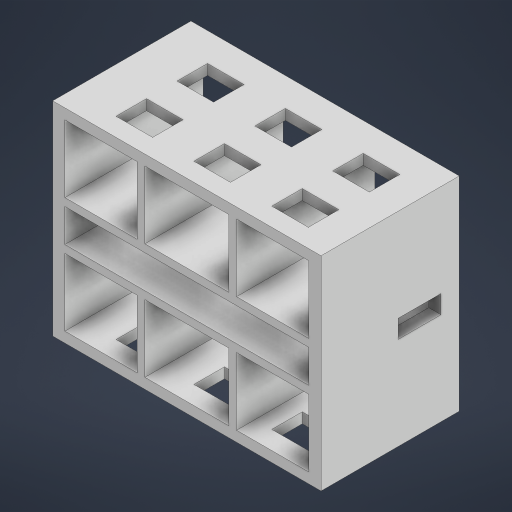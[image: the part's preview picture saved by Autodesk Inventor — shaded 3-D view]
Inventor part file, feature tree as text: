
AUTODESK INVENTOR PART (.ipt)
format: ipt  version: 2024.3 (Build 283343000, 343)  size: 326,656 bytes
history: native  units: mm
features: extrude x4, sketch x4
ambient origin geometry x8: Origin, YZ Plane, XZ Plane, XY Plane, X Axis, Y Axis, Z Axis, Center Point
bodies: Solid1 (feature_tree)
feature tree (8):
  extrude  "Extrusion1"  Depth=9000.0mm
  extrude  "Extrusion2"  Depth=10020.0mm
  extrude  "Extrusion4"  Depth=1800.0mm
  extrude  "Extrusion5"  Depth=1525.0mm
  sketch  "Sketch1"  dims[d0=12000.0mm d1=9000.0mm]
  sketch  "Sketch2"  dims[d2=13200.0mm d3=10020.0mm]
  sketch  "Sketch3"  dims[d4=6800.0mm d5=0.0mm d6=1800.0mm]
  sketch  "Sketch4"  dims[d7=1500.0mm d8=1525.0mm d9=1400.0mm d10=1800.0mm d11=1500.0mm d12=1500.0mm d13=1525.0mm d14=1800.0mm d15=1500.0mm d16=1800.0mm d17=1500.0mm d18=1500.0mm d19=1800.0mm d20=1500.0mm d21=1800.0mm d22=1500.0mm d23=1500.0mm d24=2030.0mm d25=2030.0mm d26=11000.0mm d27=0.0mm d32=90.0deg d39=3310.0mm d46=3555.0mm d47=380.0mm d50=380.0mm d52=3555.0mm d53=0.0mm d54=0.0mm d55=6800.0mm d56=0.0mm d62=450.0mm d63=2100.0mm d64=900.0mm d65=3000.0mm d66=680.0mm d67=0.0mm d28=0.5mm d29=0.872665mm d68=0.872665mm]
